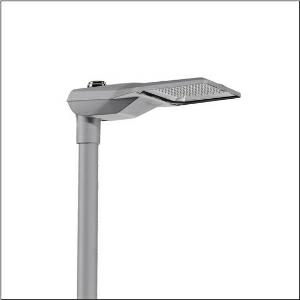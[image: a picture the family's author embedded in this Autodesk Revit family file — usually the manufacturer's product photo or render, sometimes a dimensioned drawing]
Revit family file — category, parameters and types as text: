
# Revit family: streetlight_sl_21_midi___p0_8a_5xe7u47n08nb_b7d4
name_source: partatom
category: Lighting Fixtures
units: mm (PartAtom-declared; Revit-internal decimal feet)

## family parameters
Cut with Voids When Loaded = No
Host = Face
Light Source = No
Part Type = Normal
Room Calculation Point = No
Round Connector Dimension = Use Diameter
Shared = No

## types (1)
- --- (1 x LED, 23910 lm, 151.2 W, 4000K)
    Apparent Load = 151 VA
    CIE Flux Codes = 36 69 97 100 100
    Color Rendering = 70
    Color Temperature = 4000K
    Default Elevation = 1800 mm
    Description = Streetlight SL 21 midi, mast luminaire, primary light control with lens, of PMMA, primary optical cover: cover, of toughened safety glass, transparent, light distribution: P0.8a, light emission: direct distribution, primary light characteristic: asymmetric, installation type: side-entry, LED, 3G 2.5mm², High Power LED, rated luminous flux: 23.910lm, luminous efficacy: 158lm/W, light colour: 740, colour temperature: 4000K, control gear: NEMA (7pin), control: flexible luminous flux parameterisation, time-dependent luminous flux control, constant luminous flux control, pre-setting: linear dimming characteristic, overheat protection, mains connection: 220..240V, AC, 50/60Hz, connection cable pre-assembled, cable length: 12,5m, wiring characteristics: H05VV-F, start of lifetime: 151W, end of service life: 157W, reduction: 70W, luminaire housing, of diecast aluminium (EN AC-44300), powder-coated, Siteco® metallic grey (DB 702S), corrosivity category C5 mid according to DIN EN ISO 12944, multi-level sealing system, sealing non-destructively replaceable, inclination adjustable: 0°, 5°, 10°, 15°, length: 644mm, width: 335mm, height: 110mm, spigot size: 42mm (side-entry), mounting height: 4..8m, protection rating (complete): IP66, insulation class (complete): insulation class I (protective earthing), certification: CE, ENEC, ENEC+, VDE, impact resistance: IK09, permissible operating ambient temperature for outdoor applications: -40..+50°C, standard-compliant lighting for roads and squares, packaging unit: 1 piece

Light Distribution: P0.8a
    Height = 111 mm
    Lamp = 1 x LED
    Lamp Light Flux = 23910 lm
    Lamp Power = 151.2 W
    Lamp count = 1
    Length = 644 mm
    Luminous efficacy = 158 lm/W
    Manufacturer = Siteco
    ModVariant = No
    Model = 5XE7U47N08NB
    Number of Poles = 1
    OnlyDefault = Yes
    Power Factor = 1
    Product Name = Streetlight SL 21 midi | P0.8a
    Product group = mast luminaire | pylon top
    ProductGroupID = 6100
    Protection Class = Protection class I
    Protection Degree = IP 66
    RLX_Detail_Level = 1
    RLX_Emergency_Light_Flux = 0 lm
    RLX_Emergency_Type = 0
    RLX_Emergency_Type_DB = No
    RlxData = <blob elided: 90413 chars, md5=864fecbd>
    Socket = socket
    Standby Power = 0 W
    System Light Flux = 23909 lm
    System Power = 151 W
    Type Comments = factory setting: luminous flux: 100 % | dim-lin: 254 | 802 mA
    Type Image = l_1294377.jpg
    URL = http://relux.com
    VarID = @adj_068716
    Voltage = 0 V
    Weight = 0.00 kg
    Width = 336 mm

## geometry (parser evidence)
native form markers: Blend x4, Sweep x13
no freeform markers — native parametric forms only
